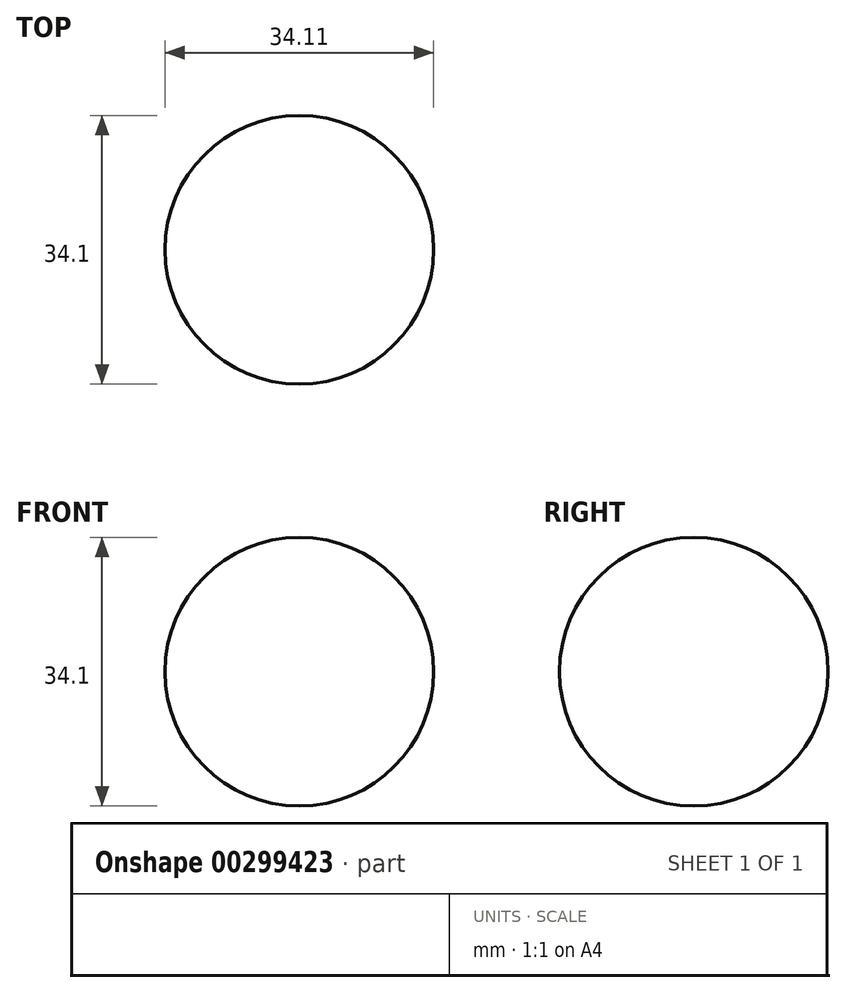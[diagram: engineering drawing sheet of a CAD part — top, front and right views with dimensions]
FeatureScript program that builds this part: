
annotation { "Feature Type Name" : "Feature", "Feature Type Description" : "" }
export const myFeature = defineFeature(function(context is Context, id is Id, definition is map)
    precondition{}
    {
        {
            var Q0;
            Q0=qCreatedBy(makeId("Top.planeOp"),FACE);
            var sketch = newSketch(context, id + "F0", { "sketchPlane" : qUnion([Q0])});
            skLineSegment(sketch, "E0", {"start": v(-59.36, 83.14) * mm, "end": v(-59.36, -9.4) * mm});
            skArc(sketch, "E1", {"start": v(-59.36, 13.09) * mm, "mid": v(-42.3, 30.14) * mm, "end": v(-59.36, 47.2) * mm});
            skSolve(sketch);
        }
        {
            var Q0;
            Q0=sQuery(id+"F0.wireOp",EDGE,"E1");
            var Q1;
            Q1=sQuery(id+"F0.wireOp",EDGE,"E0");
            revolve(context, id + "F1", {"bodyType" : ToolBodyType.SURFACE, "surfaceEntities" : qUnion([Q0]), "axis" : qUnion([Q1]), "revolveType" : RevolveType.FULL});
        }
    });
